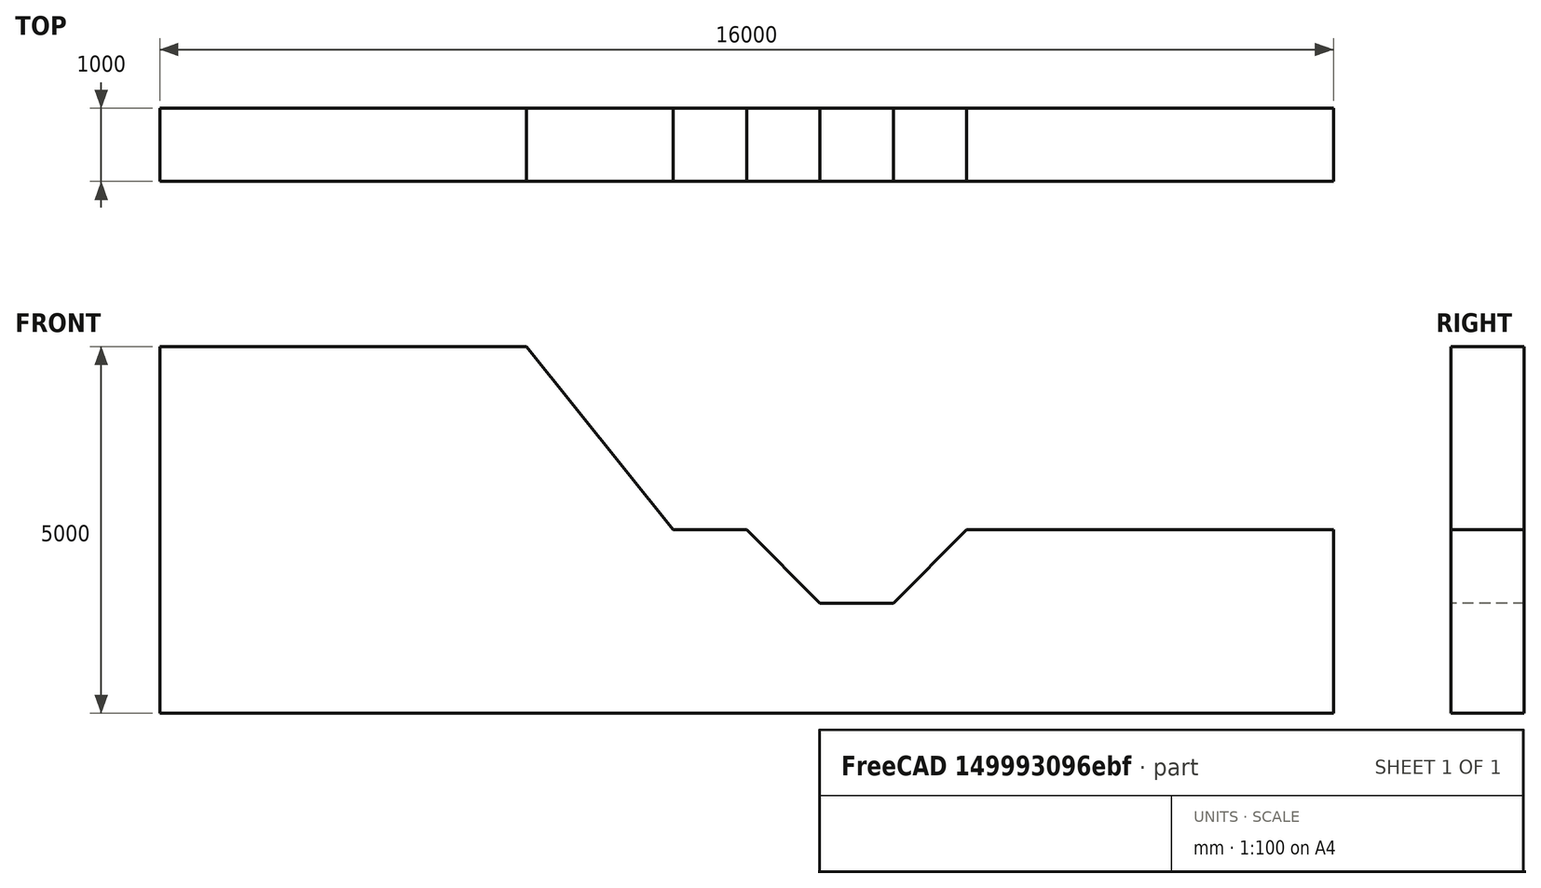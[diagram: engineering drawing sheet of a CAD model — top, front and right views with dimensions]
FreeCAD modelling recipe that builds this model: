
FCSTD DOCUMENT  (FreeCAD 0.21R33694 (Git))
Label: Embankment_with_Ditch_Example
License: All rights reserved
LicenseURL: http://en.wikipedia.org/wiki/All_rights_reserved
objects: Fem::FemMeshObjectPython×2, Sketcher::SketchObject×1, Part::Extrusion×1, Fem::FemSolverObjectPython×1, App::MaterialObjectPython×1, Fem::ConstraintFixed×1, Fem::ConstraintDisplacement×1, Fem::FemResultObjectPython×1, Fem::FemAnalysis×1
note: 2 computed .brp shape members not serialized (recipe doc carries the construction recipe); baked Part::Feature solids carry a one-line shape summary decoded from their .brp

FEATURE [Sketcher::SketchObject] Sketch
  FullyConstrained = true
  Placement = pos=(0,0,0) rot=(1,0,0;1.5708rad)
  sketch-geometry (10):
    g0: LineSegment StartX=0 StartY=0 StartZ=0 EndX=16000 EndY=0 EndZ=0
    g1: LineSegment StartX=0 StartY=0 StartZ=0 EndX=0 EndY=5000 EndZ=0
    g2: LineSegment StartX=0 StartY=5000 StartZ=0 EndX=5000 EndY=5000 EndZ=0
    g3: LineSegment StartX=5000 StartY=5000 StartZ=0 EndX=7000 EndY=2500 EndZ=0
    g4: LineSegment StartX=7000 StartY=2500 StartZ=0 EndX=8000 EndY=2500 EndZ=0
    g5: LineSegment StartX=8000 StartY=2500 StartZ=0 EndX=9000 EndY=1500 EndZ=0
    g6: LineSegment StartX=9000 StartY=1500 StartZ=0 EndX=10000 EndY=1500 EndZ=0
    g7: LineSegment StartX=10000 StartY=1500 StartZ=0 EndX=11000 EndY=2500 EndZ=0
    g8: LineSegment StartX=11000 StartY=2500 StartZ=0 EndX=16000 EndY=2500 EndZ=0
    g9: LineSegment StartX=16000 StartY=2500 StartZ=0 EndX=16000 EndY=0 EndZ=0
  constraints (29):
    c: Coincident(g0,g-1)
    c: PointOnObject(g0,g-1)
    c: Coincident(g1,g0)
    c: PointOnObject(g1,g-2)
    c: Coincident(g2,g1)
    c: Horizontal(g2)
    c: Distance(g1) = 5000
    c: Distance(g0) = 16000
    c: Distance(g2) = 5000
    c: Coincident(g3,g2)
    c: Coincident(g4,g3)
    c: Horizontal(g4)
    c: Coincident(g5,g4)
    c: Coincident(g6,g5)
    c: Horizontal(g6)
    c: Coincident(g8,g7)
    c: Horizontal(g8)
    c: Coincident(g9,g8)
    c: Coincident(g9,g0)
    c: DistanceY(g3,g2) = 2500
    c: DistanceY(g5,g4) = 1000
    c: DistanceY(g6,g7) = 1000
    c: DistanceX(g2,g3) = 2000
    c: DistanceX(g4,g5) = 1000
    c: DistanceX(g6,g7) = 1000
    c: Distance(g6) = 1000
    c: Coincident(g6,g7)
    c: Distance(g4) = 1000
    c: Distance(g8) = 5000
FEATURE [Part::Extrusion] Extrude
  Base = -> Sketch
  Dir = (0,-1,-3e-16)
  DirMode = 2
  FaceMakerClass = Part::FaceMakerBullseye
  LengthFwd = 1000
  LengthRev = 0
  Solid = true
  Symmetric = false
FEATURE [Fem::FemSolverObjectPython] SolverCcxTools  # FEM object (typed FeaturePython)
  AnalysisType = 0
  BeamShellResultOutput3D = false
  BucklingFactors = 1
  EigenmodeHighLimit = 1000000
  EigenmodeLowLimit = 0
  EigenmodesCount = 10
  GeometricalNonlinearity = 0
  IterationsControlParameterCutb = 0.25,0.5,0.75,0.85,,,1.5,
  IterationsControlParameterIter = 4,8,9,200,10,400,,200,,
  IterationsControlParameterTimeUse = false
  IterationsThermoMechMaximum = 2000
  IterationsUserDefinedIncrementations = false
  IterationsUserDefinedTimeStepLength = false
  MaterialNonlinearity = 0
  MatrixSolverType = 0
  SplitInputWriter = false
  ThermoMechSteadyState = true
  TimeEnd = 1
  TimeInitialStep = 0.01
FEATURE [Fem::FemMeshObjectPython] FEMMeshGmsh  # FEM object (typed FeaturePython)
  Algorithm2D = 0
  Algorithm3D = 0
  CharacteristicLengthMax = 1000
  CharacteristicLengthMin = 0
  CoherenceMesh = true
  ElementDimension = 0
  ElementOrder = 1
  GeometryTolerance = 1e-06
  GroupsOfNodes = false
  HighOrderOptimize = 0
  MeshSizeFromCurvature = 12
  OptimizeNetgen = false
  OptimizeStd = true
  Part = -> Extrude
  RecombinationAlgorithm = 0
  Recombine3DAll = false
  RecombineAll = false
  SecondOrderLinear = false
FEATURE [App::MaterialObjectPython] MaterialSolid  # material (typed FeaturePython)
  Category = 0
  Material = Density=2000.0000000000002 kg/m^3; Name=NoName; PoissonRatio=0.45; YoungsModulus=5000.0 kPa
  References = -> [Extrude]
FEATURE [Fem::ConstraintFixed] ConstraintFixed
  NormalDirection = (0,3e-16,-1)
  Normals = (164) [(0,3.3e-16,-1),(0,3.3e-16,-1),(0,3.3e-16,-1),(0,3.3e-16,-1),(0,3.3e-16,-1),(0,3.3e-16,-1),(0,3.3e-16,-1),(0,3.3e-16,-1),(0,3.3e-16,-1),(0,3.3e-16,-1),+154 more]
  Points = (164) [(0,-1000,-3.3e-13),(727.273,-1000,-3.3e-13),(1454.55,-1000,-3.3e-13),(2181.82,-1000,-3.3e-13),(2909.09,-1000,-3.3e-13),(3636.36,-1000,-3.3e-13),+158 more]
  References = -> [Extrude]
  Scale = 42
FEATURE [Fem::ConstraintDisplacement] ConstraintDisplacement
  NormalDirection = (0,-1,-2e-16)
  Normals = (206) [(0,-1,-2.2e-16),(0,-1,-2.2e-16),(0,-1,-2.2e-16),(0,-1,-2.2e-16),(0,-1,-2.2e-16),(0,-1,-2.2e-16),(0,-1,-2.2e-16),(0,-1,-2.2e-16),(0,-1,-2.2e-16),+197 more]
  Points = (206) [(0,-1000,-3.33e-13),(0,-1000,833.333),(0,-1000,1666.67),(0,-1000,2500),(0,-1000,3333.33),(0,-1000,4166.67),(0,-1000,5000),(800,-1000,-3.33e-13),+198 more]
  References = -> [Extrude]
  Scale = 79
  hasXFormula = false
  hasYFormula = false
  hasZFormula = false
  rotxFix = false
  rotxFree = true
  rotyFix = false
  rotyFree = true
  rotzFix = false
  rotzFree = true
  useFlowSurfaceForce = false
  xDisplacement = 0
  xFix = false
  xFree = true
  xRotation = 0
  yDisplacement = 0
  yFix = true
  yFree = false
  yRotation = 0
  zDisplacement = 0
  zFix = false
  zFree = true
  zRotation = 0
FEATURE [Fem::FemMeshObjectPython] Result_Mesh_Volume  # FEM object (typed FeaturePython)
FEATURE [Fem::FemResultObjectPython] ResultMechanical  # FEM object (typed FeaturePython)
  DisplacementLengths = [0,0,0,0,0,0,0.0123629,0.012304,1.6659,1.72526,8.34069,8.43512,6.89469,6.89397,6.64313,6.63699,4.81489,4.8147,0,0,0,0,0,0,0,0,0,0,0,0,0,0,0,0,0,0,0,0,0,0,0,0,0,0,0,0,0,0,0,0,0,0,0,0,0,0,0,0,0,0,0,0,0,0,0,0,0,0,0,0,0,0,0,0,0,0,0,0,0,0,0,0,0,+1337 more]
  DisplacementVectors = (1420) [(0,0,0),(0,0,0),(0,0,0),(0,0,0),(0,0,0),(0,0,0),(0.0109963,0,0.00565),(0.0118216,0,0.00341181),(0.579322,0,1.56193),(0.54799,0,1.63591),+1410 more]
  Eigenmode = 0
  EigenmodeFrequency = 0
  MaxShear = [0.00194562,0.00194171,0.00109108,0.00108841,0.0030504,0.00303396,0.000549628,0.000733194,0.00559312,0.00573943,0.00565195,0.00568728,0.000781109,0.00105814,0.00587386,0.00525925,0.00256807,0.00249859,0.00556097,0.00560902,3.13891e-18,+1399 more]
  Mesh = -> Result_Mesh_Volume
  NodeNumbers = [1,2,3,4,5,6,7,8,9,10,11,12,13,14,15,16,17,18,19,20,21,22,23,24,25,26,27,28,29,30,31,32,33,34,35,36,37,38,39,40,41,42,43,44,45,46,47,48,49,50,51,52,53,54,55,56,57,58,59,60,61,62,63,64,65,66,67,68,69,+1351 more]
  NodeStressXX = [-0.0189943,-0.0189426,-0.010589,-0.0105591,0.00455634,0.00455018,-0.000143079,-0.000354874,-0.0139651,-0.0132883,-0.0150797,-0.0147536,-0.0010825,-0.00171503,-0.0121659,-0.0111991,-0.00349702,-0.00342701,0.0280945,0.0310474,1.68977e-18,+1399 more]
  NodeStressXY = [-0.000331558,0.000326573,0.000175562,-0.000174052,8.44492e-05,-8.04234e-05,-7.49605e-06,-2.09327e-05,0.000520549,-0.000541092,-0.000675514,0.000483755,-1.63602e-05,3.93456e-05,-0.000200904,0.000304348,-2.18698e-05,2.87047e-05,-0.000361781,+1401 more]
  NodeStressXZ = [-0.00189168,-0.00188894,0.00106151,0.00105877,0.00293267,0.00291883,-0.000508349,-0.00065414,-0.00306786,-0.00386712,0.00258801,0.0032062,-1.28369e-06,-9.87428e-05,0.00464055,0.00475809,0.00211114,0.00202934,-0.00506471,-0.00511417,+1400 more]
  NodeStressYY = [-0.0170156,-0.0169936,-0.00955685,-0.00953384,0.00325751,0.00325525,5.82708e-05,-6.31866e-05,-0.0100211,-0.00982755,-0.0110148,-0.0104578,9.75204e-06,-0.000451228,-0.00805673,-0.00809098,-0.00182963,-0.001763,0.0272099,0.0300703,+1400 more]
  NodeStressYZ = [-0.000298799,0.000302921,-0.000178718,0.000179385,9.80238e-05,-9.72397e-05,0.000170719,-0.000213046,0.00111022,-0.000939012,0.00103785,-0.000259393,0.000257618,-0.000249291,-0.000405445,0.000275189,-0.000182248,0.000232075,-0.000387143,+1401 more]
  NodeStressZZ = [-0.0188181,-0.018821,-0.0106485,-0.0106273,0.0028954,0.00291149,8.2959e-05,0.000148887,-0.00493926,-0.00509765,-0.00534958,-0.00542685,0.000338102,0.000316735,-0.00502641,-0.0068074,-0.000597317,-0.000552226,0.0236027,0.0265298,7.85636e-18,+1399 more]
  Peeq = [0,0,0,0,0,0,0,0,0.0641586,0.0699244,0.117508,0.107147,0,0,0.00112232,0.000593042,0,0,0.0374448,0.0386131,0,0,-5.51677e-06,-0.000294187,-0.000891127,0.00648095,0.029067,0.0567027,0.0653862,0.0424476,0.00938293,-0.00133154,0,0,0,0,0,0,+1382 more]
  PrincipalMax = [-0.0169606,-0.0169401,-0.00952764,-0.00950475,0.0067784,0.00676677,0.000531665,0.000637015,-0.00386006,-0.00348825,-0.00459198,-0.00442919,0.000479464,0.000395869,-0.00270319,-0.003727,0.000526366,0.000518306,0.031391,0.0343803,7.91451e-18,+1399 more]
  PrincipalMed = [-0.0170156,-0.0169936,-0.00955685,-0.00953384,0.00325326,0.00325128,3.40774e-05,-7.68159e-05,-0.0100191,-0.00975809,-0.0109562,-0.0104053,-0.000131359,-0.000524976,-0.00809497,-0.00812499,-0.00184057,-0.00178167,0.0272471,0.030105,+1400 more]
  PrincipalMin = [-0.0208518,-0.0208235,-0.0117098,-0.0116816,0.000677594,0.000698863,-0.000567591,-0.000829373,-0.0150463,-0.0149671,-0.0158959,-0.0158037,-0.00108275,-0.00172041,-0.0144509,-0.0142455,-0.00460977,-0.00447887,0.0202691,0.0231623,1.63669e-18,+1399 more]
  ResultType = Fem::ResultMechanical
  Stats = [0,0,0,0,0,0,0,0,0,0,0,0,0,0,0,0,0,0,0,0,0,0,0,0,0,0]
  Time = 0
  vonMises = [0.00386403,0.00385693,0.0021677,0.00216241,0.00530474,0.00527698,0.000953405,0.00127008,0.00970409,0.00995513,0.00981534,0.00985489,0.00136359,0.00183789,0.0101852,0.00914992,0.00445257,0.00433224,0.00973556,0.00980622,5.43676e-18,+1399 more]
FEATURE [Fem::FemAnalysis] Analysis
  Group = -> [SolverCcxTools,FEMMeshGmsh,MaterialSolid,ConstraintFixed,ConstraintDisplacement,ResultMechanical]
